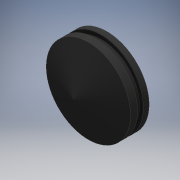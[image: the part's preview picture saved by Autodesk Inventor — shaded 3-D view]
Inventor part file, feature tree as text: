
AUTODESK INVENTOR PART (.ipt)
format: ipt  version: 2018 (Build 220112000, 112)  size: 140,800 bytes
history: native  units: mm
features: revolve x2, sketch x2
ambient origin geometry x8: Origin, YZ Plane, XZ Plane, XY Plane, X Axis, Y Axis, Z Axis, Center Point
bodies: Solid1 (feature_tree)
feature tree (4):
  revolve  "Revolution1"  [1 undecoded]
  revolve  "Revolution2"  [1 undecoded]
  sketch  "Sketch1"  dims[d0=3.490659mm d1=10.0mm]
  sketch  "Sketch2"  dims[d2=1.5mm d3=1.5mm d4=1.85mm d5=11.0mm d6=90.0deg d7=6.0mm d8=3.0mm d9=7.5mm d10=3.0mm d11=6.0mm d12=90.0deg]
note: 2 required parameter values undecoded (feature->parameter linkage not recoverable at this tier; creation-order binding heuristic only, values carry confidence <= 0.55)
